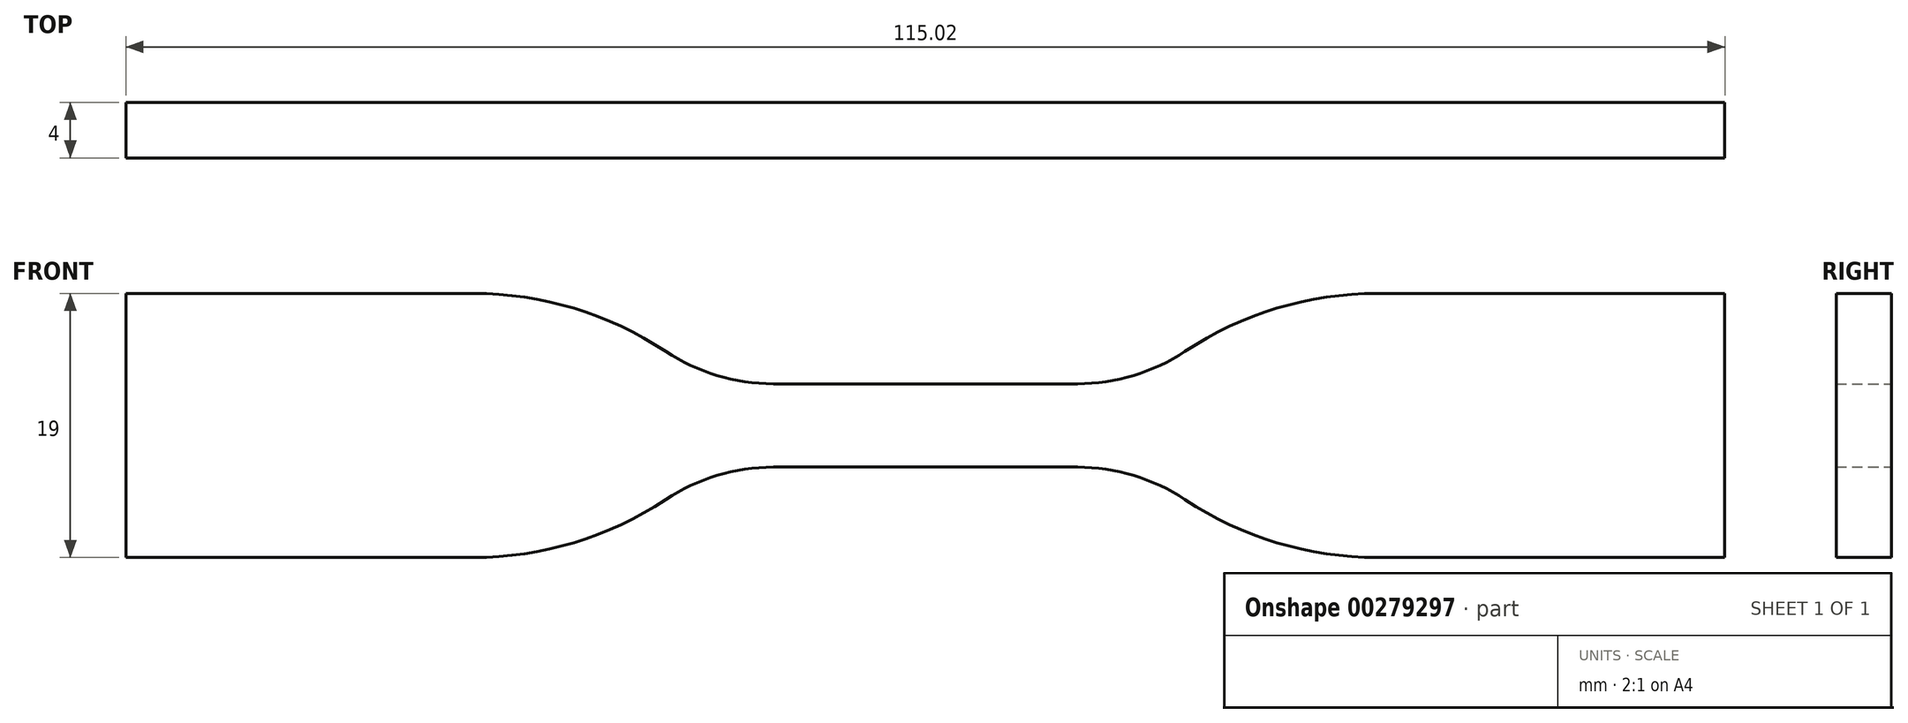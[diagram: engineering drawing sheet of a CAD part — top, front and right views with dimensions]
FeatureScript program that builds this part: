
annotation { "Feature Type Name" : "Feature", "Feature Type Description" : "" }
export const myFeature = defineFeature(function(context is Context, id is Id, definition is map)
    precondition{}
    {
        {
            var Q0;
            Q0=qCreatedBy(makeId("Front.planeOp"),FACE);
            var sketch = newSketch(context, id + "F0", { "sketchPlane" : qUnion([Q0])});
            skLineSegment(sketch, "E0", {"start": v(0, 3) * mm, "end": v(15.68, 3) * mm});
            skLineSegment(sketch, "E1", {"start": v(32.5, 9.5) * mm, "end": v(57.5, 9.5) * mm});
            skLineSegment(sketch, "E2", {"start": v(57.5, 9.5) * mm, "end": v(57.5, 0) * mm});
            skLineSegment(sketch, "E3.MirrorCS", {"start": v(0, -3) * mm, "end": v(15.68, -3) * mm});
            skLineSegment(sketch, "E4.MirrorCS", {"start": v(57.5, -9.5) * mm, "end": v(57.5, 0) * mm});
            skLineSegment(sketch, "E5.MirrorCS", {"start": v(32.5, -9.5) * mm, "end": v(57.5, -9.5) * mm});
            skLineSegment(sketch, "E6.MirrorCS", {"start": v(0, 3) * mm, "end": v(10.94, 3) * mm});
            skLineSegment(sketch, "E7.MirrorCS", {"start": v(0, -3) * mm, "end": v(10.94, -3) * mm});
            skLineSegment(sketch, "E8.MirrorCS", {"start": v(-32.5, -9.5) * mm, "end": v(-57.5, -9.5) * mm});
            skLineSegment(sketch, "E9.MirrorCS", {"start": v(0, 3) * mm, "end": v(-15.68, 3) * mm});
            skLineSegment(sketch, "E10.MirrorCS", {"start": v(-32.5, 9.5) * mm, "end": v(-57.5, 9.5) * mm});
            skLineSegment(sketch, "E11.MirrorCS", {"start": v(-57.5, -9.5) * mm, "end": v(-57.5, 0) * mm});
            skLineSegment(sketch, "E12.MirrorCS", {"start": v(-57.5, 9.5) * mm, "end": v(-57.5, 0) * mm});
            skLineSegment(sketch, "E13.MirrorCS", {"start": v(0, -3) * mm, "end": v(-10.94, -3) * mm});
            skLineSegment(sketch, "E14.MirrorCS", {"start": v(0, -3) * mm, "end": v(-15.68, -3) * mm});
            skLineSegment(sketch, "E15.MirrorCS", {"start": v(0, 3) * mm, "end": v(-10.94, 3) * mm});
            skArc(sketch, "E16", {"start": v(32.5, 9.5) * mm, "mid": v(25.28, 8.43) * mm, "end": v(18.68, 5.33) * mm});
            skArc(sketch, "E17", {"start": v(-18.68, 5.33) * mm, "mid": v(-25.28, 8.43) * mm, "end": v(-32.5, 9.5) * mm});
            skArc(sketch, "E18", {"start": v(-32.5, -9.5) * mm, "mid": v(-25.28, -8.43) * mm, "end": v(-18.68, -5.33) * mm});
            skArc(sketch, "E19", {"start": v(18.68, -5.33) * mm, "mid": v(25.28, -8.43) * mm, "end": v(32.5, -9.5) * mm});
            skPoint(sketch, "E20.visualSharp", {"position": v(-15.68, 3) * mm});
            skArc(sketch, "E20.filletArc", {"start": v(-18.68, 5.33) * mm, "mid": v(-14.98, 3.6) * mm, "end": v(-10.94, 3) * mm});
            skPoint(sketch, "E21.visualSharp", {"position": v(15.68, 3) * mm});
            skArc(sketch, "E21.filletArc", {"start": v(10.94, 3) * mm, "mid": v(14.98, 3.6) * mm, "end": v(18.68, 5.33) * mm});
            skPoint(sketch, "E22.visualSharp", {"position": v(-15.68, -3) * mm});
            skArc(sketch, "E22.filletArc", {"start": v(-10.94, -3) * mm, "mid": v(-14.98, -3.6) * mm, "end": v(-18.68, -5.33) * mm});
            skPoint(sketch, "E23.visualSharp", {"position": v(15.68, -3) * mm});
            skArc(sketch, "E23.filletArc", {"start": v(18.68, -5.33) * mm, "mid": v(14.98, -3.6) * mm, "end": v(10.94, -3) * mm});
            skSolve(sketch);
        }
        {
            var Q0;
            Q0 = qSketchRegion(id + "F0", true);
            extrude(context, id + "F1", {"entities" : qUnion([Q0]), "endBound" : BoundingType.SYMMETRIC, "depth" : 4 * mm});
        }
    });
